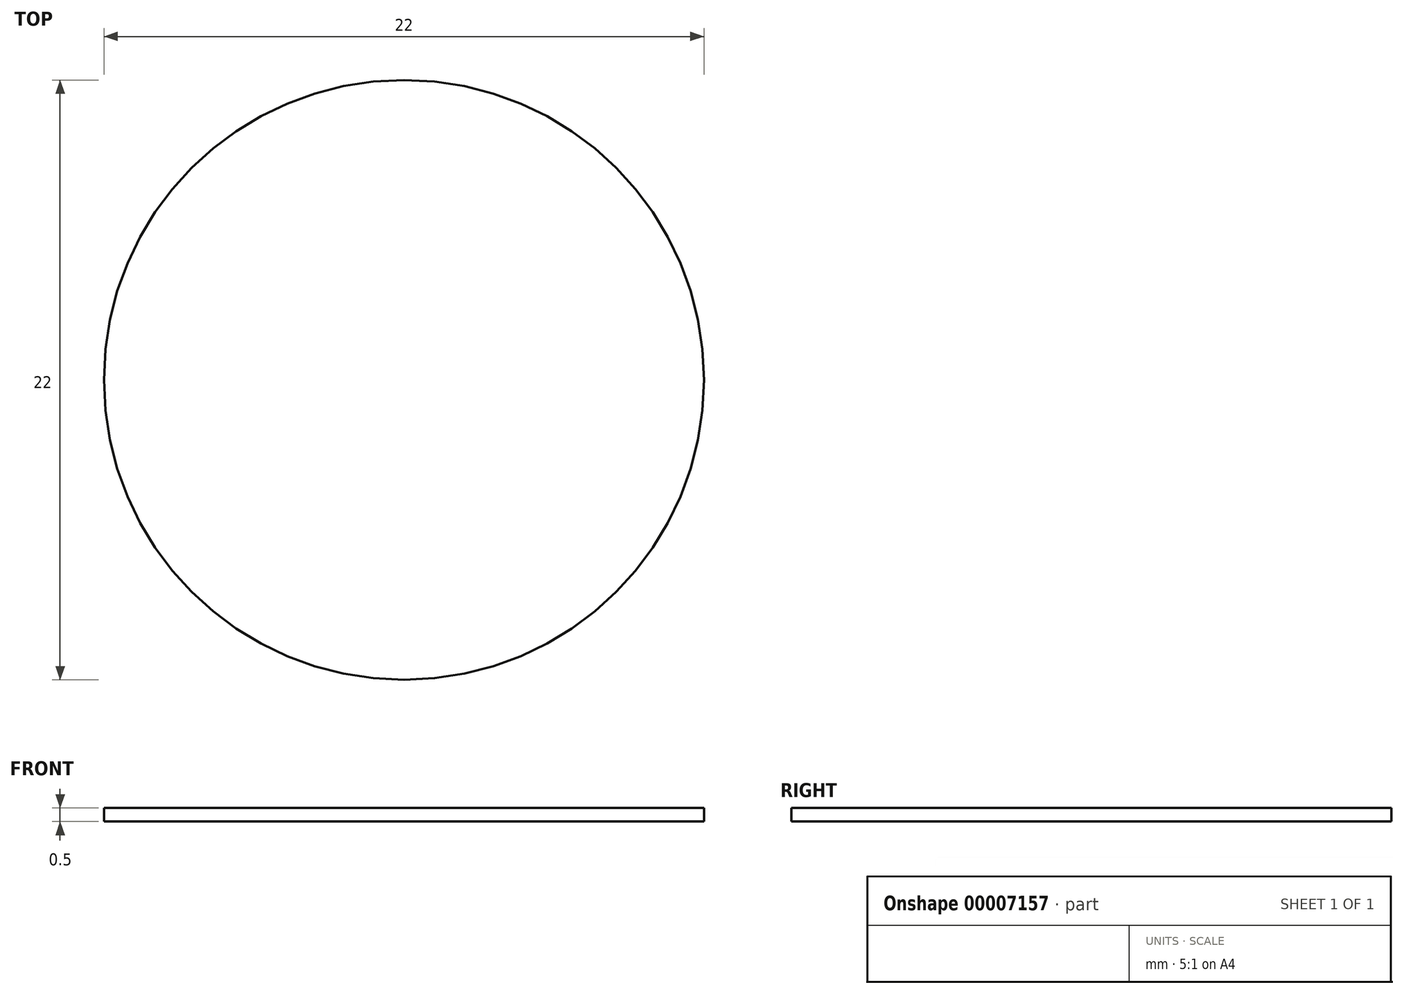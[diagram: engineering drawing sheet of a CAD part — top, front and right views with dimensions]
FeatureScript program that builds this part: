
annotation { "Feature Type Name" : "Feature", "Feature Type Description" : "" }
export const myFeature = defineFeature(function(context is Context, id is Id, definition is map)
    precondition{}
    {
        {
            var Q0;
            Q0=qCreatedBy(makeId("Top.planeOp"),FACE);
            var sketch = newSketch(context, id + "F0", { "sketchPlane" : qUnion([Q0])});
            skCircle(sketch, "E0", {"center": v(0, 0) * mm, "radius": 11 * mm});
            skSolve(sketch);
        }
        {
            var Q0;
            Q0=makeQuery(id+"F0.imprint","IMPRINT",FACE,{"disambiguationData":[TD([[makeQuery(id+"F0.imprint","IMPRINT",EDGE,{"derivedFrom":sQuery(id+"F0.wireOp",EDGE,"E0")}),1.0]])]});
            extrude(context, id + "F1", {"entities" : qUnion([Q0]), "depth" : .5 * mm});
        }
    });
